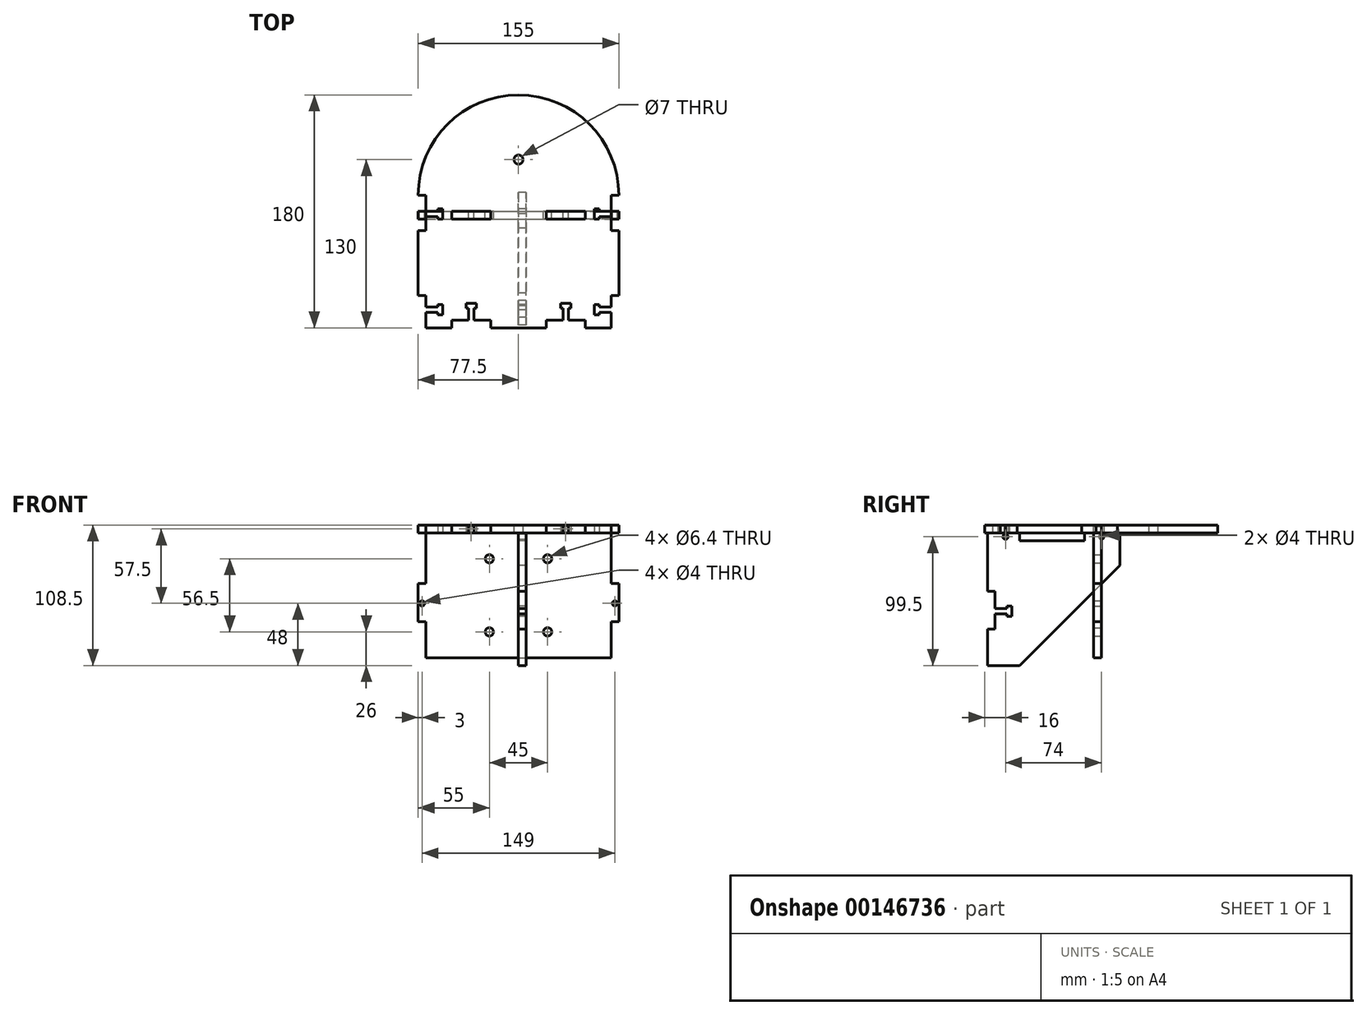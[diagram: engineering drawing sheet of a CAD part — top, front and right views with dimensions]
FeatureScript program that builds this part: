
annotation { "Feature Type Name" : "Feature", "Feature Type Description" : "" }
export const myFeature = defineFeature(function(context is Context, id is Id, definition is map)
    precondition{}
    {
        {
            var Q0;
            Q0=qCreatedBy(makeId("Top.planeOp"),FACE);
            var sketch = newSketch(context, id + "F0", { "sketchPlane" : qUnion([Q0])});
            skLineSegment(sketch, "E0.bottom", {"start": v(0, 90) * mm, "end": v(0, 90) * mm});
            skPoint(sketch, "E0.middle", {"position": v(0, 0) * mm});
            skPoint(sketch, "E1.visualSharp", {"position": v(-77.5, 90) * mm});
            skArc(sketch, "E1.filletArc", {"start": v(0, 90) * mm, "mid": v(-54.8, 67.3) * mm, "end": v(-77.5, 12.5) * mm});
            skPoint(sketch, "E2.visualSharp", {"position": v(77.5, 90) * mm});
            skLineSegment(sketch, "E3", {"start": v(-71.5, 12.5) * mm, "end": v(-77.5, 12.5) * mm});
            skLineSegment(sketch, "E4", {"start": v(-62.5, 0) * mm, "end": v(-62.5, 2) * mm});
            skLineSegment(sketch, "E5", {"start": v(-62.5, 2) * mm, "end": v(-58.5, 2) * mm});
            skLineSegment(sketch, "E6", {"start": v(-58.5, 2) * mm, "end": v(-58.5, -6) * mm});
            skLineSegment(sketch, "E7", {"start": v(-58.5, -6) * mm, "end": v(-62.5, -6) * mm});
            skLineSegment(sketch, "E8", {"start": v(-62.5, -6) * mm, "end": v(-62.5, -4) * mm});
            skLineSegment(sketch, "E9", {"start": v(-77.5, -15) * mm, "end": v(-71.5, -15) * mm});
            skLineSegment(sketch, "E10", {"start": v(-77.5, -65) * mm, "end": v(-71.5, -65) * mm});
            skLineSegment(sketch, "E11", {"start": v(-62.5, 0) * mm, "end": v(-71.5, 0) * mm});
            skLineSegment(sketch, "E12", {"start": v(-62.5, -4) * mm, "end": v(-71.5, -4) * mm});
            skLineSegment(sketch, "E13", {"start": v(-71.5, 12.5) * mm, "end": v(-71.5, 0) * mm});
            skLineSegment(sketch, "E14", {"start": v(-71.5, -4) * mm, "end": v(-71.5, -15) * mm});
            skLineSegment(sketch, "E15", {"start": v(-62.5, -74) * mm, "end": v(-62.5, -72) * mm});
            skLineSegment(sketch, "E16", {"start": v(-62.5, -72) * mm, "end": v(-58.5, -72) * mm});
            skLineSegment(sketch, "E17", {"start": v(-58.5, -72) * mm, "end": v(-58.5, -80) * mm});
            skLineSegment(sketch, "E18", {"start": v(-58.5, -80) * mm, "end": v(-62.5, -80) * mm});
            skLineSegment(sketch, "E19", {"start": v(-62.5, -80) * mm, "end": v(-62.5, -78) * mm});
            skLineSegment(sketch, "E20", {"start": v(-62.5, -78) * mm, "end": v(-71.5, -78) * mm});
            skLineSegment(sketch, "E21", {"start": v(-62.5, -74) * mm, "end": v(-71.5, -74) * mm});
            skLineSegment(sketch, "E22", {"start": v(-71.5, -65) * mm, "end": v(-71.5, -74) * mm});
            skLineSegment(sketch, "E23", {"start": v(-71.5, -78) * mm, "end": v(-71.5, -90) * mm});
            skLineSegment(sketch, "E24", {"start": v(-77.5, -15) * mm, "end": v(-77.5, -65) * mm});
            skLineSegment(sketch, "E25", {"start": v(0, 90) * mm, "end": v(0, -90) * mm, "construction": true});
            skArc(sketch, "E26.MirrorCS", {"start": v(0, 90) * mm, "mid": v(54.8, 67.3) * mm, "end": v(77.5, 12.5) * mm});
            skLineSegment(sketch, "E27.MirrorCS", {"start": v(71.5, 12.5) * mm, "end": v(77.5, 12.5) * mm});
            skLineSegment(sketch, "E28.MirrorCS", {"start": v(71.5, 12.5) * mm, "end": v(71.5, 0) * mm});
            skLineSegment(sketch, "E29.MirrorCS", {"start": v(62.5, 0) * mm, "end": v(71.5, 0) * mm});
            skLineSegment(sketch, "E30.MirrorCS", {"start": v(62.5, 2) * mm, "end": v(58.5, 2) * mm});
            skLineSegment(sketch, "E31.MirrorCS", {"start": v(62.5, 0) * mm, "end": v(62.5, 2) * mm});
            skLineSegment(sketch, "E32.MirrorCS", {"start": v(58.5, 2) * mm, "end": v(58.5, -6) * mm});
            skLineSegment(sketch, "E33.MirrorCS", {"start": v(58.5, -6) * mm, "end": v(62.5, -6) * mm});
            skLineSegment(sketch, "E34.MirrorCS", {"start": v(62.5, -6) * mm, "end": v(62.5, -4) * mm});
            skLineSegment(sketch, "E35.MirrorCS", {"start": v(62.5, -4) * mm, "end": v(71.5, -4) * mm});
            skLineSegment(sketch, "E36.MirrorCS", {"start": v(71.5, -4) * mm, "end": v(71.5, -15) * mm});
            skLineSegment(sketch, "E37.MirrorCS", {"start": v(77.5, -15) * mm, "end": v(77.5, -65) * mm});
            skLineSegment(sketch, "E38.MirrorCS", {"start": v(71.5, -65) * mm, "end": v(71.5, -74) * mm});
            skLineSegment(sketch, "E39.MirrorCS", {"start": v(62.5, -74) * mm, "end": v(71.5, -74) * mm});
            skLineSegment(sketch, "E40.MirrorCS", {"start": v(62.5, -74) * mm, "end": v(62.5, -72) * mm});
            skLineSegment(sketch, "E41.MirrorCS", {"start": v(62.5, -72) * mm, "end": v(58.5, -72) * mm});
            skLineSegment(sketch, "E42.MirrorCS", {"start": v(58.5, -72) * mm, "end": v(58.5, -80) * mm});
            skLineSegment(sketch, "E43.MirrorCS", {"start": v(58.5, -80) * mm, "end": v(62.5, -80) * mm});
            skLineSegment(sketch, "E44.MirrorCS", {"start": v(62.5, -80) * mm, "end": v(62.5, -78) * mm});
            skLineSegment(sketch, "E45.MirrorCS", {"start": v(62.5, -78) * mm, "end": v(71.5, -78) * mm});
            skLineSegment(sketch, "E46.MirrorCS", {"start": v(71.5, -78) * mm, "end": v(71.5, -90) * mm});
            skLineSegment(sketch, "E47.MirrorCS", {"start": v(77.5, -15) * mm, "end": v(71.5, -15) * mm});
            skLineSegment(sketch, "E48.MirrorCS", {"start": v(77.5, -65) * mm, "end": v(71.5, -65) * mm});
            skCircle(sketch, "E49", {"center": v(0, 40) * mm, "radius": 3.5 * mm});
            skLineSegment(sketch, "E50", {"start": v(-51.5, -90) * mm, "end": v(-51.5, -84) * mm});
            skLineSegment(sketch, "E51", {"start": v(-21.5, -84) * mm, "end": v(-21.5, -90) * mm});
            skLineSegment(sketch, "E52", {"start": v(-71.5, -90) * mm, "end": v(-51.5, -90) * mm});
            skLineSegment(sketch, "E53", {"start": v(-21.5, -90) * mm, "end": v(0, -90) * mm});
            skLineSegment(sketch, "E54", {"start": v(-38.5, -84) * mm, "end": v(-38.5, -75) * mm});
            skLineSegment(sketch, "E55", {"start": v(-38.5, -75) * mm, "end": v(-40.5, -75) * mm});
            skLineSegment(sketch, "E56", {"start": v(-40.5, -75) * mm, "end": v(-40.5, -71) * mm});
            skLineSegment(sketch, "E57", {"start": v(-40.5, -71) * mm, "end": v(-32.5, -71) * mm});
            skLineSegment(sketch, "E58", {"start": v(-32.5, -71) * mm, "end": v(-32.5, -75) * mm});
            skLineSegment(sketch, "E59", {"start": v(-32.5, -75) * mm, "end": v(-34.5, -75) * mm});
            skLineSegment(sketch, "E60", {"start": v(-34.5, -75) * mm, "end": v(-34.5, -84) * mm});
            skLineSegment(sketch, "E61", {"start": v(-51.5, -84) * mm, "end": v(-38.5, -84) * mm});
            skLineSegment(sketch, "E62", {"start": v(-34.5, -84) * mm, "end": v(-21.5, -84) * mm});
            skLineSegment(sketch, "E63.MirrorCS", {"start": v(38.5, -75) * mm, "end": v(40.5, -75) * mm});
            skLineSegment(sketch, "E64.MirrorCS", {"start": v(32.5, -75) * mm, "end": v(34.5, -75) * mm});
            skLineSegment(sketch, "E65.MirrorCS", {"start": v(40.5, -71) * mm, "end": v(32.5, -71) * mm});
            skLineSegment(sketch, "E66.MirrorCS", {"start": v(40.5, -75) * mm, "end": v(40.5, -71) * mm});
            skLineSegment(sketch, "E67.MirrorCS", {"start": v(51.5, -90) * mm, "end": v(51.5, -84) * mm});
            skLineSegment(sketch, "E68.MirrorCS", {"start": v(34.5, -84) * mm, "end": v(21.5, -84) * mm});
            skLineSegment(sketch, "E69.MirrorCS", {"start": v(38.5, -84) * mm, "end": v(38.5, -75) * mm});
            skLineSegment(sketch, "E70.MirrorCS", {"start": v(51.5, -84) * mm, "end": v(38.5, -84) * mm});
            skLineSegment(sketch, "E71.MirrorCS", {"start": v(34.5, -75) * mm, "end": v(34.5, -84) * mm});
            skLineSegment(sketch, "E72.MirrorCS", {"start": v(32.5, -71) * mm, "end": v(32.5, -75) * mm});
            skLineSegment(sketch, "E73.MirrorCS", {"start": v(21.5, -84) * mm, "end": v(21.5, -90) * mm});
            skLineSegment(sketch, "E74", {"start": v(71.5, -90) * mm, "end": v(51.5, -90) * mm});
            skLineSegment(sketch, "E75", {"start": v(21.5, -90) * mm, "end": v(0, -90) * mm});
            skSolve(sketch);
        }
        {
            var Q0;
            Q0=qCreatedBy(makeId("Right.planeOp"),FACE);
            var sketch = newSketch(context, id + "F1", { "sketchPlane" : qUnion([Q0])});
            skLineSegment(sketch, "E76", {"start": v(-88, 0) * mm, "end": v(-63, 0) * mm});
            skLineSegment(sketch, "E77", {"start": v(-63, 0) * mm, "end": v(-63, -6) * mm});
            skLineSegment(sketch, "E78", {"start": v(-63, -6) * mm, "end": v(-13, -6) * mm});
            skLineSegment(sketch, "E79", {"start": v(-13, -6) * mm, "end": v(-13, 0) * mm});
            skLineSegment(sketch, "E80", {"start": v(-13, 0) * mm, "end": v(14.5, 0) * mm});
            skLineSegment(sketch, "E81", {"start": v(-88, -102.5) * mm, "end": v(-63, -102.5) * mm});
            skLineSegment(sketch, "E82", {"start": v(14.5, -25) * mm, "end": v(14.5, 0) * mm});
            skLineSegment(sketch, "E83", {"start": v(14.5, -25) * mm, "end": v(-63, -102.5) * mm});
            skLineSegment(sketch, "E84", {"start": v(-13, -6) * mm, "end": v(14.5, -6) * mm, "construction": true});
            skPoint(sketch, "E84.endSnap0", {"position": v(14.5, -12.5) * mm});
            skLineSegment(sketch, "E85", {"start": v(-63, -6) * mm, "end": v(-88, -6) * mm, "construction": true});
            skCircle(sketch, "E86", {"center": v(0, -3) * mm, "radius": 2 * mm});
            skCircle(sketch, "E87", {"center": v(-74, -3) * mm, "radius": 2 * mm});
            skLineSegment(sketch, "E88", {"start": v(-88, -74.5) * mm, "end": v(-82, -74.5) * mm});
            skLineSegment(sketch, "E89", {"start": v(-82, -45) * mm, "end": v(-88, -45) * mm});
            skLineSegment(sketch, "E90", {"start": v(-88, -102.5) * mm, "end": v(-88, -74.5) * mm});
            skLineSegment(sketch, "E91", {"start": v(-88, -45) * mm, "end": v(-88, 0) * mm});
            skLineSegment(sketch, "E92", {"start": v(-73, -58.5) * mm, "end": v(-73, -56.5) * mm});
            skLineSegment(sketch, "E93", {"start": v(-73, -56.5) * mm, "end": v(-69, -56.5) * mm});
            skLineSegment(sketch, "E94", {"start": v(-69, -56.5) * mm, "end": v(-69, -64.5) * mm});
            skLineSegment(sketch, "E95", {"start": v(-69, -64.5) * mm, "end": v(-73, -64.5) * mm});
            skLineSegment(sketch, "E96", {"start": v(-73, -64.5) * mm, "end": v(-73, -62.5) * mm});
            skLineSegment(sketch, "E97", {"start": v(-73, -62.5) * mm, "end": v(-82, -62.5) * mm});
            skLineSegment(sketch, "E98", {"start": v(-82, -58.44) * mm, "end": v(-73, -58.5) * mm});
            skLineSegment(sketch, "E99", {"start": v(-82, -74.5) * mm, "end": v(-82, -62.5) * mm});
            skLineSegment(sketch, "E100", {"start": v(-82, -58.44) * mm, "end": v(-82, -45) * mm});
            skSolve(sketch);
        }
        {
            var Q0;
            Q0 = qSketchRegion(id + "F0", true);
            extrude(context, id + "F2", {"entities" : qUnion([Q0]), "depth" : 6 * mm});
        }
        {
            var Q0;
            Q0=qCreatedBy(makeId("Front.planeOp"),FACE);
            var sketch = newSketch(context, id + "F3", { "sketchPlane" : qUnion([Q0])});
            skLineSegment(sketch, "E101", {"start": v(-71.5, -96.5) * mm, "end": v(71.5, -96.5) * mm});
            skLineSegment(sketch, "E102", {"start": v(-71.5, 0) * mm, "end": v(-51.5, 0) * mm});
            skLineSegment(sketch, "E103", {"start": v(-51.5, 0) * mm, "end": v(-51.5, 6) * mm});
            skLineSegment(sketch, "E104", {"start": v(-51.5, 6) * mm, "end": v(-21.5, 6) * mm});
            skLineSegment(sketch, "E105", {"start": v(-21.5, 6) * mm, "end": v(-21.5, 0) * mm});
            skLineSegment(sketch, "E106", {"start": v(71.5, 0) * mm, "end": v(51.5, 0) * mm});
            skLineSegment(sketch, "E107", {"start": v(51.5, 0) * mm, "end": v(51.5, 6) * mm});
            skLineSegment(sketch, "E108", {"start": v(51.5, 6) * mm, "end": v(21.5, 6) * mm});
            skLineSegment(sketch, "E109", {"start": v(21.5, 6) * mm, "end": v(21.5, 0) * mm});
            skLineSegment(sketch, "E110", {"start": v(-21.5, 0) * mm, "end": v(21.5, 0) * mm});
            skLineSegment(sketch, "E111", {"start": v(-71.5, -39) * mm, "end": v(-77.5, -39) * mm});
            skLineSegment(sketch, "E112", {"start": v(-77.5, -39) * mm, "end": v(-77.5, -68.5) * mm});
            skLineSegment(sketch, "E113", {"start": v(-77.5, -68.5) * mm, "end": v(-71.5, -68.5) * mm});
            skLineSegment(sketch, "E114", {"start": v(-71.5, -68.5) * mm, "end": v(-71.5, -96.5) * mm});
            skLineSegment(sketch, "E115", {"start": v(-71.5, -39) * mm, "end": v(-71.5, 0) * mm});
            skLineSegment(sketch, "E116", {"start": v(71.5, 0) * mm, "end": v(71.5, -39) * mm});
            skLineSegment(sketch, "E117", {"start": v(71.5, -39) * mm, "end": v(77.5, -39) * mm});
            skLineSegment(sketch, "E118", {"start": v(77.5, -39) * mm, "end": v(77.5, -68.5) * mm});
            skLineSegment(sketch, "E119", {"start": v(77.5, -68.5) * mm, "end": v(71.5, -68.5) * mm});
            skLineSegment(sketch, "E120", {"start": v(71.5, -68.5) * mm, "end": v(71.5, -96.5) * mm});
            skCircle(sketch, "E121", {"center": v(-74.5, -54.5) * mm, "radius": 2 * mm});
            skCircle(sketch, "E122", {"center": v(74.5, -54.5) * mm, "radius": 2 * mm});
            skCircle(sketch, "E123", {"center": v(-36.5, 3) * mm, "radius": 2 * mm});
            skCircle(sketch, "E124", {"center": v(36.5, 3) * mm, "radius": 2 * mm});
            skCircle(sketch, "E125", {"center": v(-22.5, -20) * mm, "radius": 3.2 * mm});
            skCircle(sketch, "E126", {"center": v(-22.5, -76.5) * mm, "radius": 3.2 * mm});
            skCircle(sketch, "E127", {"center": v(22.5, -20) * mm, "radius": 3.2 * mm});
            skCircle(sketch, "E128", {"center": v(22.5, -76.5) * mm, "radius": 3.2 * mm});
            skSolve(sketch);
        }
        {
            var Q0;
            Q0=makeQuery(id+"F1.imprint","IMPRINT",FACE,{"disambiguationData":[TD([[makeQuery(id+"F1.imprint","IMPRINT",EDGE,{"derivedFrom":sQuery(id+"F1.wireOp",EDGE,"E76")}),-1.0]])]});
            extrude(context, id + "F4", {"entities" : qUnion([Q0]), "depth" : 6 * mm});
        }
        {
            var Q0;
            Q0=makeQuery(id+"F3.imprint","IMPRINT",FACE,{"disambiguationData":[TD([[makeQuery(id+"F3.imprint","IMPRINT",EDGE,{"derivedFrom":sQuery(id+"F3.wireOp",EDGE,"E101")}),1.0]])]});
            extrude(context, id + "F5", {"entities" : qUnion([Q0]), "depth" : 6 * mm});
        }
    });
